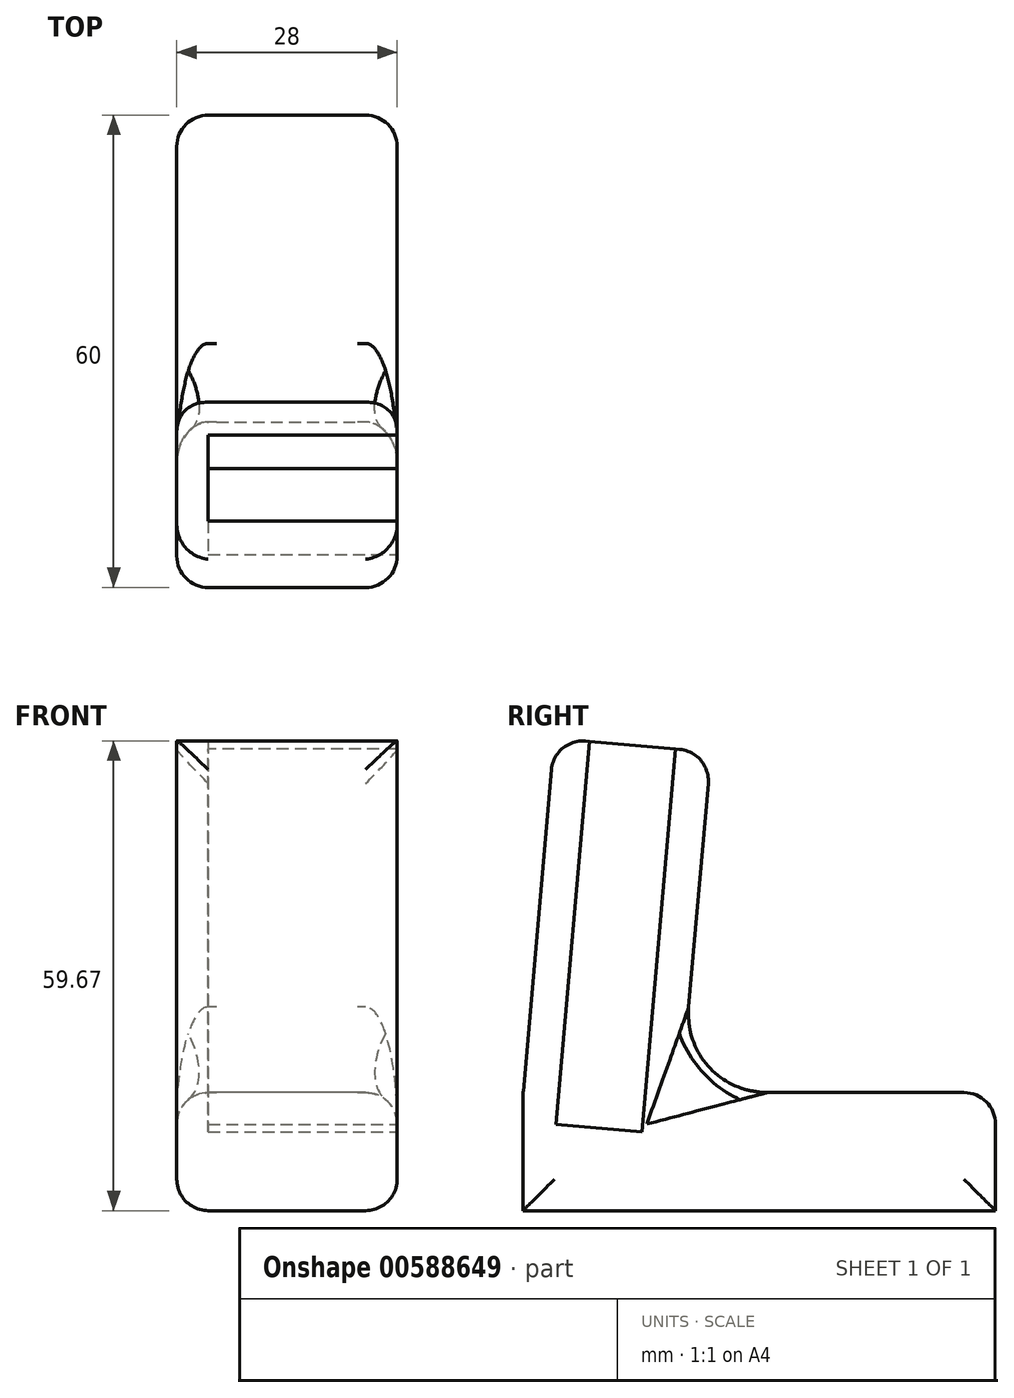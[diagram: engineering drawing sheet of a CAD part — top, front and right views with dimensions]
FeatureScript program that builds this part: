
annotation { "Feature Type Name" : "Feature", "Feature Type Description" : "" }
export const myFeature = defineFeature(function(context is Context, id is Id, definition is map)
    precondition{}
    {
        {
            var Q0;
            Q0=qCreatedBy(makeId("Right.planeOp"),FACE);
            var sketch = newSketch(context, id + "F0", { "sketchPlane" : qUnion([Q0])});
            skLineSegment(sketch, "E0.bottom", {"start": v(-60, 0) * mm, "end": v(0, 0) * mm});
            skLineSegment(sketch, "E0.top", {"start": v(-60, 15) * mm, "end": v(0, 15) * mm});
            skLineSegment(sketch, "E0.left", {"start": v(-60, 0) * mm, "end": v(-60, 15) * mm});
            skLineSegment(sketch, "E0.right", {"start": v(0, 0) * mm, "end": v(0, 15) * mm});
            skLineSegment(sketch, "E1", {"start": v(-39.92, 15) * mm, "end": v(-60, 15) * mm});
            skLineSegment(sketch, "E2", {"start": v(-60, 15) * mm, "end": v(-56.06, 60) * mm});
            skLineSegment(sketch, "E3", {"start": v(-56.06, 60) * mm, "end": v(-36.14, 58.26) * mm});
            skLineSegment(sketch, "E4", {"start": v(-36.14, 58.26) * mm, "end": v(-39.92, 15) * mm});
            skSolve(sketch);
        }
        {
            var Q0;
            Q0 = qSketchRegion(id + "F0", true);
            extrude(context, id + "F1", {"entities" : qUnion([Q0]), "endBound" : BoundingType.SYMMETRIC, "depth" : 28 * mm, "offsetDistance" : 25 * mm});
        }
        {
            var Q0;
            Q0=makeQuery(id+"F1.opExtrude","CAP_FACE",FACE,{"disambiguationData":[OSD([sQuery(id+"F0.wireOp",EDGE,"E0.bottom"),sQuery(id+"F0.wireOp",EDGE,"E0.top"),sQuery(id+"F0.wireOp",EDGE,"E0.left"),sQuery(id+"F0.wireOp",EDGE,"E0.right"),sQuery(id+"F0.wireOp",EDGE,"E2"),sQuery(id+"F0.wireOp",EDGE,"E3"),sQuery(id+"F0.wireOp",EDGE,"E4")])],"isStart":false});
            var sketch = newSketch(context, id + "F2", { "sketchPlane" : qUnion([Q0])});
            skLineSegment(sketch, "E5", {"start": v(-50.88, 67.66) * mm, "end": v(-55.84, 10.96) * mm});
            skLineSegment(sketch, "E6", {"start": v(-55.84, 10.96) * mm, "end": v(-44.88, 10) * mm});
            skLineSegment(sketch, "E7", {"start": v(-44.88, 10) * mm, "end": v(-39.92, 66.7) * mm});
            skLineSegment(sketch, "E8", {"start": v(-39.92, 66.7) * mm, "end": v(-50.88, 67.66) * mm});
            skLineSegment(sketch, "E9", {"start": v(-53.36, 39.31) * mm, "end": v(-57.84, 39.7) * mm, "construction": true});
            skLineSegment(sketch, "E10", {"start": v(-42.4, 38.35) * mm, "end": v(-37.91, 37.96) * mm, "construction": true});
            skSolve(sketch);
        }
        {
            var Q0;
            Q0 = qSketchRegion(id + "F2", true);
            extrude(context, id + "F3", {"entities" : qUnion([Q0]), "operationType" : NewBodyOperationType.REMOVE, "oppositeDirection" : true, "depth" : 24 * mm, "offsetDistance" : 25 * mm});
        }
        {
            var Q0;
            Q0=makeQuery(id+"F1.opExtrude","CAP_EDGE",EDGE,{"disambiguationData":[OSD([sQuery(id+"F0.wireOp",EDGE,"E0.left")])],"isStart":false});
            var Q1;
            Q1=makeQuery(id+"F1.opExtrude","SWEPT_EDGE",EDGE,{"disambiguationData":[OSD([sQuery(id+"F0.wireOp",EDGE,"E0.left"),sQuery(id+"F0.wireOp",EDGE,"E1"),sQuery(id+"F0.wireOp",EDGE,"E2")])]});
            var Q2;
            Q2=makeQuery(id+"F1.opExtrude","CAP_EDGE",EDGE,{"disambiguationData":[OSD([sQuery(id+"F0.wireOp",EDGE,"E2")])],"isStart":false});
            var Q3;
            Q3=makeQuery(id+"F1.opExtrude","CAP_EDGE",EDGE,{"disambiguationData":[OSD([sQuery(id+"F0.wireOp",EDGE,"E0.left")])],"isStart":true});
            var Q4;
            Q4=makeQuery(id+"F1.opExtrude","CAP_EDGE",EDGE,{"disambiguationData":[OSD([sQuery(id+"F0.wireOp",EDGE,"E2")])],"isStart":true});
            var Q5;
            Q5=makeQuery(id+"F1.opExtrude","SWEPT_EDGE",EDGE,{"disambiguationData":[OSD([sQuery(id+"F0.wireOp",EDGE,"E2"),sQuery(id+"F0.wireOp",EDGE,"E3")])]});
            var Q6;
            Q6=makeQuery(id+"F1.opExtrude","CAP_EDGE",EDGE,{"disambiguationData":[OSD([sQuery(id+"F0.wireOp",EDGE,"E4")])],"isStart":true});
            var Q7;
            Q7=makeQuery(id+"F1.opExtrude","CAP_EDGE",EDGE,{"disambiguationData":[OSD([sQuery(id+"F0.wireOp",EDGE,"E0.top")])],"isStart":true});
            var Q8;
            Q8=makeQuery(id+"F1.opExtrude","CAP_EDGE",EDGE,{"disambiguationData":[OSD([sQuery(id+"F0.wireOp",EDGE,"E0.bottom")])],"isStart":true});
            var Q9;
            Q9=makeQuery(id+"F1.opExtrude","CAP_EDGE",EDGE,{"disambiguationData":[OSD([sQuery(id+"F0.wireOp",EDGE,"E0.right")])],"isStart":true});
            var Q10;
            Q10=makeQuery(id+"F1.opExtrude","CAP_EDGE",EDGE,{"disambiguationData":[OSD([sQuery(id+"F0.wireOp",EDGE,"E0.right")])],"isStart":false});
            var Q11;
            Q11=makeQuery(id+"F1.opExtrude","SWEPT_EDGE",EDGE,{"disambiguationData":[OSD([sQuery(id+"F0.wireOp",EDGE,"E0.top"),sQuery(id+"F0.wireOp",EDGE,"E0.right")])]});
            var Q12;
            Q12=makeQuery(id+"F1.opExtrude","CAP_EDGE",EDGE,{"disambiguationData":[OSD([sQuery(id+"F0.wireOp",EDGE,"E0.top")])],"isStart":false});
            var Q13;
            Q13=makeQuery(id+"F1.opExtrude","CAP_EDGE",EDGE,{"disambiguationData":[OSD([sQuery(id+"F0.wireOp",EDGE,"E0.bottom")])],"isStart":false});
            var Q14;
            Q14=makeQuery(id+"F1.opExtrude","CAP_EDGE",EDGE,{"disambiguationData":[OSD([sQuery(id+"F0.wireOp",EDGE,"E4")])],"isStart":false});
            var Q15;
            Q15=makeQuery(id+"F1.opExtrude","SWEPT_EDGE",EDGE,{"disambiguationData":[OSD([sQuery(id+"F0.wireOp",EDGE,"E3"),sQuery(id+"F0.wireOp",EDGE,"E4")])]});
            fillet(context, id + "F4", {"entities" : qUnion([Q0, Q1, Q2, Q3, Q4, Q5, Q6, Q7, Q8, Q9, Q10, Q11, Q12, Q13, Q14, Q15]), "radius" : 4 * mm, "tangentPropagation" : true, "allowEdgeOverflow" : false});
        }
        {
            var Q0;
            Q0=makeQuery(id+"F1.opExtrude","SWEPT_EDGE",EDGE,{"disambiguationData":[OSD([sQuery(id+"F0.wireOp",EDGE,"E0.top"),sQuery(id+"F0.wireOp",EDGE,"E1"),sQuery(id+"F0.wireOp",EDGE,"E4")])]});
            fillet(context, id + "F5", {"entities" : qUnion([Q0]), "radius" : 10 * mm, "tangentPropagation" : true, "allowEdgeOverflow" : false});
        }
    });
